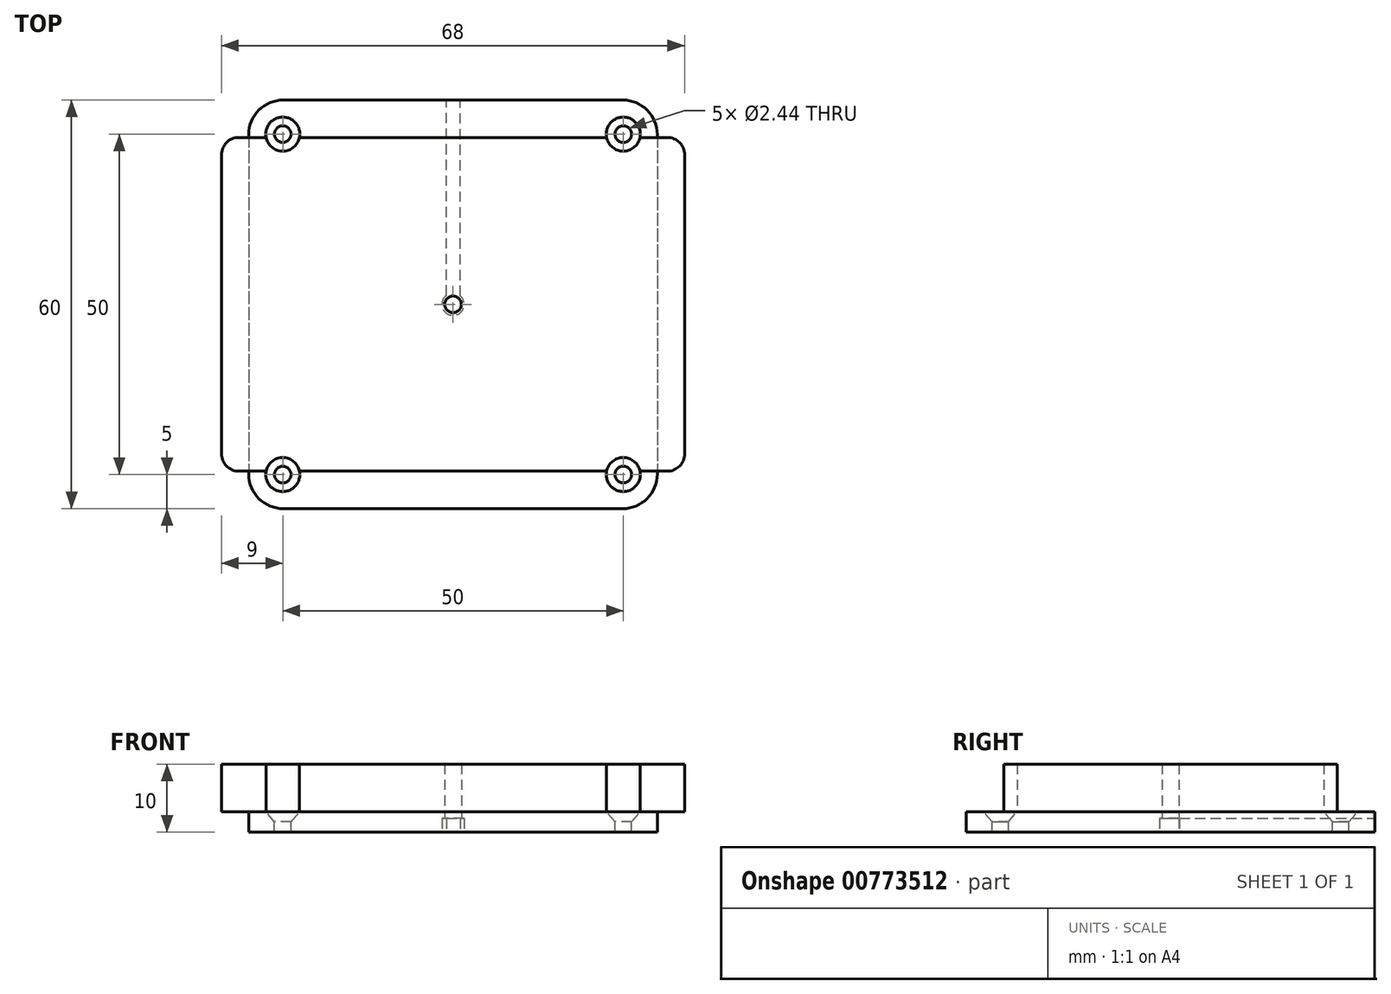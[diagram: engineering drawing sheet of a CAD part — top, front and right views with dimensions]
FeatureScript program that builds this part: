
annotation { "Feature Type Name" : "Feature", "Feature Type Description" : "" }
export const myFeature = defineFeature(function(context is Context, id is Id, definition is map)
    precondition{}
    {
        {
            var Q0;
            Q0=qCreatedBy(makeId("Top.planeOp"),FACE);
            var sketch = newSketch(context, id + "F0", { "sketchPlane" : qUnion([Q0])});
            skLineSegment(sketch, "E0.bottom", {"start": v(30, 30) * mm, "end": v(-30, 30) * mm});
            skLineSegment(sketch, "E0.top", {"start": v(30, -30) * mm, "end": v(-30, -30) * mm});
            skLineSegment(sketch, "E0.left", {"start": v(30, 30) * mm, "end": v(30, -30) * mm});
            skLineSegment(sketch, "E0.right", {"start": v(-30, 30) * mm, "end": v(-30, -30) * mm});
            skPoint(sketch, "E0.middle", {"position": v(0, 0) * mm});
            skSolve(sketch);
        }
        {
            var Q0;
            Q0=makeQuery(id+"F0.imprint","IMPRINT",FACE,{"disambiguationData":[TD([[makeQuery(id+"F0.imprint","IMPRINT",EDGE,{"derivedFrom":sQuery(id+"F0.wireOp",EDGE,"E0.bottom")}),1.0]])]});
            extrude(context, id + "F1", {"entities" : qUnion([Q0]), "depth" : 3 * mm, "offsetDistance" : 25.4 * mm});
        }
        {
            var Q0;
            {var subQ0=sQuery(id+"F0.wireOp",EDGE,"E0.right");var subQ1=sQuery(id+"F0.wireOp",EDGE,"E0.left");var subQ2=sQuery(id+"F0.wireOp",EDGE,"E0.top");Q0=makeQuery(id+"F6.boolean.opBoolean","SPLIT",FACE,{"disambiguationData":[TD([makeQuery(id+"F1.opExtrude","SWEPT_FACE",FACE,{"disambiguationData":[OSD([subQ2])]})])],"derivedFrom":makeQuery(id+"F1.opExtrude","CAP_FACE",FACE,{"disambiguationData":[OSD([sQuery(id+"F0.wireOp",EDGE,"E0.bottom"),subQ2,subQ1,subQ0])],"isStart":false})});}
            var sketch = newSketch(context, id + "F2", { "sketchPlane" : qUnion([Q0])});
            skLineSegment(sketch, "E1.bottom", {"start": v(25, 25) * mm, "end": v(-25, 25) * mm, "construction": true});
            skLineSegment(sketch, "E1.top", {"start": v(25, -25) * mm, "end": v(-25, -25) * mm, "construction": true});
            skLineSegment(sketch, "E1.left", {"start": v(25, 25) * mm, "end": v(25, -25) * mm, "construction": true});
            skLineSegment(sketch, "E1.right", {"start": v(-25, 25) * mm, "end": v(-25, -25) * mm, "construction": true});
            skPoint(sketch, "E1.middle", {"position": v(0, 0) * mm});
            skPoint(sketch, "E2", {"position": v(-15.21, 16.06) * mm});
            skPoint(sketch, "E3", {"position": v(16.64, 15.11) * mm});
            skPoint(sketch, "E4", {"position": v(13.42, -12.26) * mm});
            skPoint(sketch, "E5", {"position": v(-13.84, -15.57) * mm});
            skSolve(sketch);
        }
        {
            var Q0;
            Q0=sQuery(id+"F2.wireOp",VERTEX,"E1.bottom.end");
            var Q1;
            Q1=sQuery(id+"F2.wireOp",VERTEX,"E1.top.end");
            var Q2;
            Q2=sQuery(id+"F2.wireOp",VERTEX,"E1.top.start");
            var Q3;
            Q3=sQuery(id+"F2.wireOp",VERTEX,"E1.bottom.start");
            var Q4;
            Q4=makeQuery(id+"F1.opExtrude","SWEPT_BODY",BODY,{"disambiguationData":[OSD([sQuery(id+"F0.wireOp",EDGE,"E0.bottom"),sQuery(id+"F0.wireOp",EDGE,"E0.top"),sQuery(id+"F0.wireOp",EDGE,"E0.left"),sQuery(id+"F0.wireOp",EDGE,"E0.right")])]});
            hole(context, id + "F3", {"style" : HoleStyle.C_SINK, "endStyle" : HoleEndStyle.BLIND, "standardTappedOrClearance" : lookupTablePath({ "standard" : "ANSI", "fit" : "Normal (ASME)", "size" : "#2", "type" : "Clearance" }), "standardBlindInLast" : lookupTablePath({ "fit" : "Free", "standard" : "ANSI", "size" : "#2", "type" : "Clearance" }), "holeDiameter" : 2.44 * mm, "cSinkDiameter" : 5 * mm, "cSinkAngle" : 82 * degree, "majorDiameter" : 6.35 * mm, "holeDepth" : 12.7 * mm, "isTappedThrough" : true, "tappedDepth" : 12.7 * mm, "tapClearance" : 3, "locations" : qUnion([Q0, Q1, Q2, Q3]), "scope" : qUnion([Q4])});
        }
        {
            var Q0;
            Q0=makeQuery(id+"F1.opExtrude","SWEPT_EDGE",EDGE,{"disambiguationData":[OSD([sQuery(id+"F0.wireOp",EDGE,"E0.top"),sQuery(id+"F0.wireOp",EDGE,"E0.left")])]});
            var Q1;
            Q1=makeQuery(id+"F1.opExtrude","SWEPT_EDGE",EDGE,{"disambiguationData":[OSD([sQuery(id+"F0.wireOp",EDGE,"E0.top"),sQuery(id+"F0.wireOp",EDGE,"E0.right")])]});
            var Q2;
            Q2=makeQuery(id+"F1.opExtrude","SWEPT_EDGE",EDGE,{"disambiguationData":[OSD([sQuery(id+"F0.wireOp",EDGE,"E0.bottom"),sQuery(id+"F0.wireOp",EDGE,"E0.left")])]});
            var Q3;
            Q3=makeQuery(id+"F1.opExtrude","SWEPT_EDGE",EDGE,{"disambiguationData":[OSD([sQuery(id+"F0.wireOp",EDGE,"E0.bottom"),sQuery(id+"F0.wireOp",EDGE,"E0.right")])]});
            fillet(context, id + "F4", {"entities" : qUnion([Q0, Q1, Q2, Q3]), "radius" : 5.08 * mm, "tangentPropagation" : true, "allowEdgeOverflow" : false});
        }
        {
            var Q0;
            Q0=makeQuery(id+"F1.opExtrude","CAP_FACE",FACE,{"disambiguationData":[OSD([sQuery(id+"F0.wireOp",EDGE,"E0.bottom"),sQuery(id+"F0.wireOp",EDGE,"E0.top"),sQuery(id+"F0.wireOp",EDGE,"E0.left"),sQuery(id+"F0.wireOp",EDGE,"E0.right")])],"isStart":false});
            var sketch = newSketch(context, id + "F5", { "sketchPlane" : qUnion([Q0])});
            skLineSegment(sketch, "E6.bottom", {"start": v(34, 24.5) * mm, "end": v(-34, 24.5) * mm});
            skLineSegment(sketch, "E6.top", {"start": v(34, -24.5) * mm, "end": v(-34, -24.5) * mm});
            skLineSegment(sketch, "E6.left", {"start": v(34, 24.5) * mm, "end": v(34, -24.5) * mm});
            skLineSegment(sketch, "E6.right", {"start": v(-34, 24.5) * mm, "end": v(-34, -24.5) * mm});
            skPoint(sketch, "E6.middle", {"position": v(0, 0) * mm});
            skSolve(sketch);
        }
        {
            var Q0;
            {var subQ0=sQuery(id+"F5.wireOp",EDGE,"E6.left");Q0=makeQuery(id+"F5.imprint","IMPRINT",FACE,{"disambiguationData":[TD([[makeQuery(id+"F5.imprint","IMPRINT",EDGE,{"derivedFrom":subQ0}),-1.0]])]});}
            var Q1;
            {var subQ0=sQuery(id+"F5.wireOp",EDGE,"E6.bottom");var subQ1=makeQuery(id+"F1.opExtrude","CAP_EDGE",EDGE,{"disambiguationData":[OSD([sQuery(id+"F0.wireOp",EDGE,"E0.left")])],"isStart":false});var subQ2=makeQuery(id+"F5.imprint","INTERSECT",VERTEX,{"derivedFrom":[subQ1,subQ0]});Q1=makeQuery(id+"F5.imprint","IMPRINT",FACE,{"disambiguationData":[TD([[makeQuery(id+"F5.imprint","IMPRINT",EDGE,{"disambiguationData":[TD([[subQ2,-1.0]])],"derivedFrom":subQ0}),1.0]])]});}
            var Q2;
            {var subQ0=sQuery(id+"F5.wireOp",EDGE,"E6.right");Q2=makeQuery(id+"F5.imprint","IMPRINT",FACE,{"disambiguationData":[TD([[makeQuery(id+"F5.imprint","IMPRINT",EDGE,{"derivedFrom":subQ0}),1.0]])]});}
            extrude(context, id + "F6", {"entities" : qUnion([Q0, Q1, Q2]), "operationType" : NewBodyOperationType.ADD, "depth" : 7 * mm, "offsetDistance" : 25.4 * mm});
        }
        {
            var Q0;
            Q0=makeQuery(id+"F6.opExtrude","SWEPT_EDGE",EDGE,{"disambiguationData":[OSD([sQuery(id+"F5.wireOp",EDGE,"E6.top"),sQuery(id+"F5.wireOp",EDGE,"E6.right")])]});
            var Q1;
            Q1=makeQuery(id+"F6.opExtrude","SWEPT_EDGE",EDGE,{"disambiguationData":[OSD([sQuery(id+"F5.wireOp",EDGE,"E6.top"),sQuery(id+"F5.wireOp",EDGE,"E6.left")])]});
            var Q2;
            Q2=makeQuery(id+"F6.opExtrude","SWEPT_EDGE",EDGE,{"disambiguationData":[OSD([sQuery(id+"F5.wireOp",EDGE,"E6.bottom"),sQuery(id+"F5.wireOp",EDGE,"E6.left")])]});
            var Q3;
            Q3=makeQuery(id+"F6.opExtrude","SWEPT_EDGE",EDGE,{"disambiguationData":[OSD([sQuery(id+"F5.wireOp",EDGE,"E6.bottom"),sQuery(id+"F5.wireOp",EDGE,"E6.right")])]});
            fillet(context, id + "F7", {"entities" : qUnion([Q0, Q1, Q2, Q3]), "radius" : 2.54 * mm, "tangentPropagation" : true, "allowEdgeOverflow" : false});
        }
        {
            var Q0;
            Q0=sQuery(id+"F0.wireOp",VERTEX,"E0.middle");
            var Q1;
            Q1=makeQuery(id+"F1.opExtrude","SWEPT_BODY",BODY,{"disambiguationData":[OSD([sQuery(id+"F0.wireOp",EDGE,"E0.bottom"),sQuery(id+"F0.wireOp",EDGE,"E0.top"),sQuery(id+"F0.wireOp",EDGE,"E0.left"),sQuery(id+"F0.wireOp",EDGE,"E0.right")])]});
            hole(context, id + "F8", {"style" : HoleStyle.SIMPLE, "endStyle" : HoleEndStyle.THROUGH, "oppositeDirection" : true, "holeDiameter" : 2.44 * mm, "majorDiameter" : 6.35 * mm, "isTappedThrough" : true, "tappedDepth" : 12.7 * mm, "tapClearance" : 3, "locations" : qUnion([Q0]), "scope" : qUnion([Q1])});
        }
        {
            var Q0;
            Q0=makeQuery(id+"F1.opExtrude","CAP_FACE",FACE,{"disambiguationData":[OSD([sQuery(id+"F0.wireOp",EDGE,"E0.bottom"),sQuery(id+"F0.wireOp",EDGE,"E0.top"),sQuery(id+"F0.wireOp",EDGE,"E0.left"),sQuery(id+"F0.wireOp",EDGE,"E0.right")])],"isStart":true});
            var sketch = newSketch(context, id + "F9", { "sketchPlane" : qUnion([Q0])});
            skSolve(sketch);
        }
        {
            var Q0;
            {var subQ1=sQuery(id+"F0.wireOp",EDGE,"E0.bottom");Q0=makeQuery(id+"F9.imprint","IMPRINT",FACE,{"disambiguationData":[TD([[makeQuery(id+"F9.imprint","IMPRINT",EDGE,{"derivedFrom":makeQuery(id+"F1.opExtrude","CAP_EDGE",EDGE,{"disambiguationData":[OSD([subQ1])],"isStart":true})}),-1.0]])]});}
            var sketch = newSketch(context, id + "F10", { "sketchPlane" : qUnion([Q0])});
            skLineSegment(sketch, "E7.top", {"start": v(-0.96, -31.34) * mm, "end": v(1.04, -31.34) * mm});
            skLineSegment(sketch, "E7.left", {"start": v(-0.96, -1.31) * mm, "end": v(-0.96, -31.34) * mm});
            skLineSegment(sketch, "E7.right", {"start": v(1.04, -1.25) * mm, "end": v(1.04, -31.34) * mm});
            skArc(sketch, "E8", {"start": v(1.04, -1.25) * mm, "mid": v(-0.05, 1.63) * mm, "end": v(-0.96, -1.31) * mm});
            skSolve(sketch);
        }
        {
            var Q0;
            Q0 = qSketchRegion(id + "F10", true);
            extrude(context, id + "F11", {"entities" : qUnion([Q0]), "operationType" : NewBodyOperationType.REMOVE, "oppositeDirection" : true, "depth" : 2 * mm, "offsetDistance" : 25.4 * mm});
        }
    });
